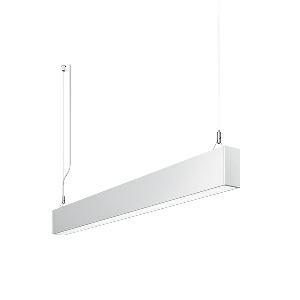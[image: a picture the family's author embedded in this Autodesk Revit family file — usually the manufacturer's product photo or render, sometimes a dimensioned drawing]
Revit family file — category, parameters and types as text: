
# Revit family: dotoo_line_-_dlp_2000_830_d_00805805_164c
name_source: partatom
category: Lighting Fixtures
units: mm (PartAtom-declared; Revit-internal decimal feet)

## family parameters
Cut with Voids When Loaded = No
Host = Face
Light Source = No
Part Type = Normal
Room Calculation Point = No
Round Connector Dimension = Use Diameter
Shared = No

## types (1)
- DOTOO.line - DLP 2000/830/D (1 x LED, 1650 lm, 3000K)
    Apparent Load = 16 VA
    Approval mark = CE
    CIE Flux Codes = 67 91 98 100 100
    Color Rendering = 80-89
    Color Temperature = 3000K
    Control Gear = Electronic ballast
    Default Elevation = 1800 mm
    Description = DLP 2000/830/D|Suspended luminaire|light source: LED|connected load: 220-240 V, 50/60 Hz|Power consumption: approx. 16 W|standby: approx. 0,15|luminous flux: 1650 lm|luminous efficacy: 103 lm/W|light distribution: Direct|direct ratio: approx. 100 %|colour temperature: Warm white, ca. 3000 K|color rendering index (CRI): >= 80|chromaticity tolerance:  3 SDCM|System of protection: IP 40|technology: Continuously dimmable|luminaire body|material: Sectional aluminium|colour: White|lamp cover: Acrylic (PMMA), Clear|mains lead: 2.00 m With free stranded wires|Fastening: Steel cable 0.3 - 0.7 m|glare control: Prism aperture|luminance(L65): <= 3000 cd/m|unified glare rating(4H 8H): <=  19|special features: DALI Load 1x, TouchDIM - dimming via standard switch, Flicker-free, Suitable as emergency lighting|
    Frequency = 50 Hz
    Height = 110 mm
    Lamp = 1 x LED
    Lamp Light Flux = 1650 lm
    Lamp count = 1
    Length = 1414 mm
    Luminous efficacy = 103 lm/W
    Manufacturer = Waldmann
    ModVariant = No
    Model = 00805805
    Mounting Place = Ceiling
    Mounting Type = Pendant
    Number of Poles = 1
    OnlyDefault = Yes
    Power Factor = 1
    Product Name = DOTOO.line - DLP 2000/830/D
    Product group = Suspended luminaire
    ProductGroupID = 9
    Protection Class = Protection class I
    Protection Degree = IP 40
    RLX_Detail_Level = 1
    RLX_Emergency_Light_Flux = 0 lm
    RLX_Emergency_Type = 0
    RLX_Emergency_Type_DB = No
    RlxData = <blob elided: 19641 chars, md5=d7245ab5>
    Socket = socket
    Standby Power = 0 W
    System Light Flux = 1650 lm
    System Power = 16 W
    Type Comments = Product without accessories
    Type Image = 113291000-00692522.jpg
    URL = http://relux.com
    VarID = ---
    Voltage = 230 V
    Voltage Range = 220-240 V
    Weight = 0.00 kg
    Width = 60 mm  [stored 0.19685 ft]

note: [stored X ft] marks values corroborated as IEEE doubles in the binary element streams (Revit-internal decimal feet)

## geometry (parser evidence)
native form markers: Blend x4, Sweep x11
no freeform markers — native parametric forms only
